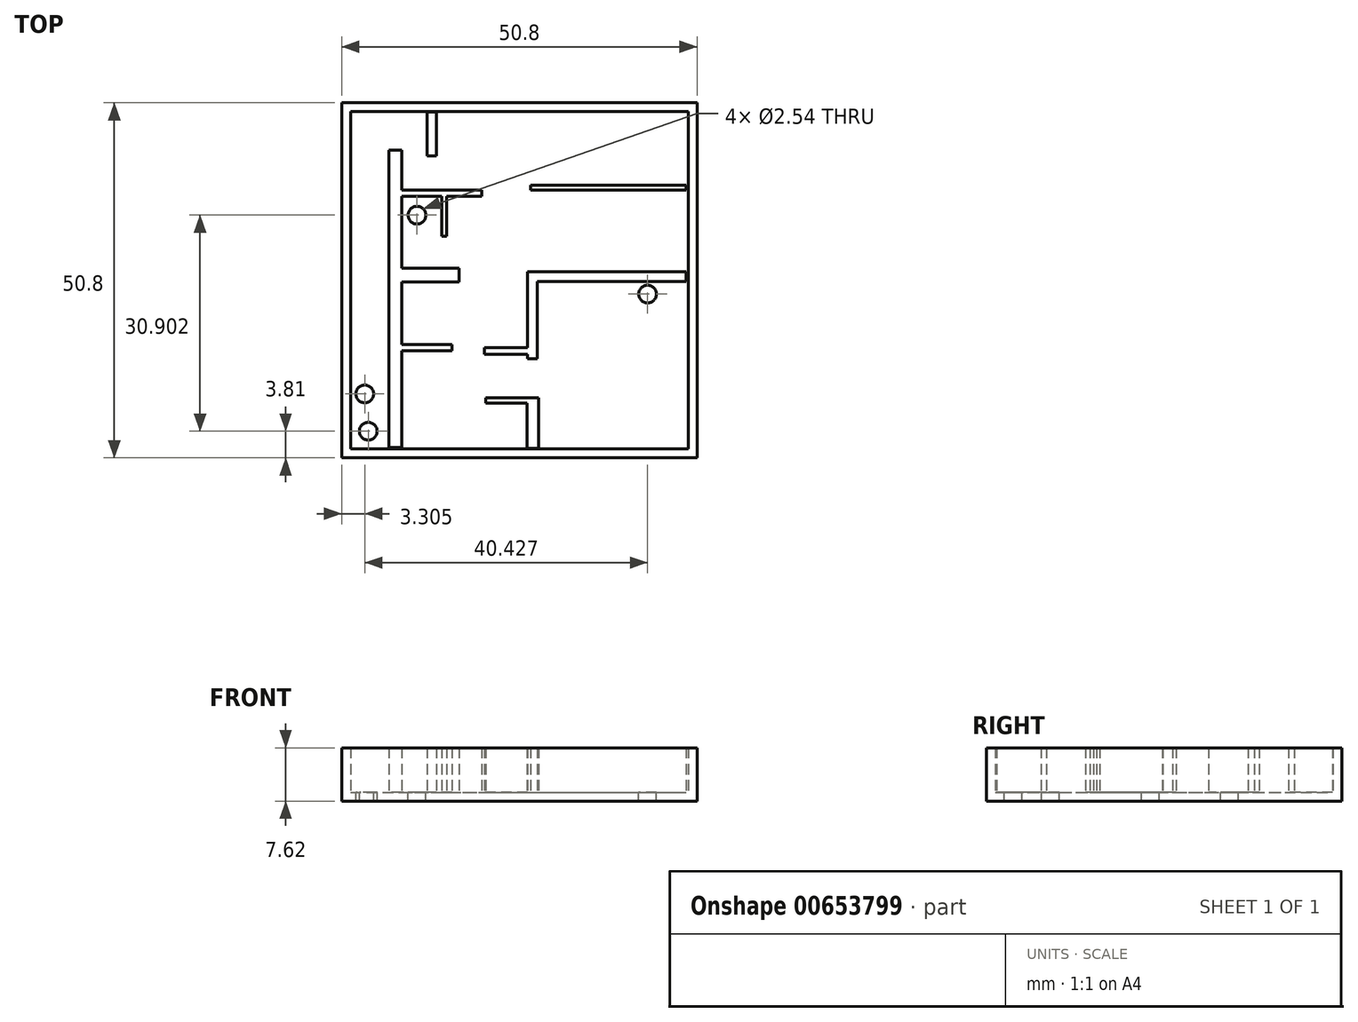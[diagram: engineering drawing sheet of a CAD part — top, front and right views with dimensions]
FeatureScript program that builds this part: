
annotation { "Feature Type Name" : "Feature", "Feature Type Description" : "" }
export const myFeature = defineFeature(function(context is Context, id is Id, definition is map)
    precondition{}
    {
        {
            var Q0;
            Q0=qCreatedBy(makeId("Top.planeOp"),FACE);
            var sketch = newSketch(context, id + "F0", { "sketchPlane" : qUnion([Q0])});
            skLineSegment(sketch, "E0.bottom", {"start": v(0, 0) * mm, "end": v(50.8, 0) * mm});
            skLineSegment(sketch, "E0.top", {"start": v(0, 50.8) * mm, "end": v(50.8, 50.8) * mm});
            skLineSegment(sketch, "E0.left", {"start": v(0, 0) * mm, "end": v(0, 50.8) * mm});
            skLineSegment(sketch, "E0.right", {"start": v(50.8, 0) * mm, "end": v(50.8, 50.8) * mm});
            skSolve(sketch);
        }
        {
            var Q0;
            Q0=makeQuery(id+"F0.imprint","IMPRINT",FACE,{"disambiguationData":[TD([[makeQuery(id+"F0.imprint","IMPRINT",EDGE,{"derivedFrom":sQuery(id+"F0.wireOp",EDGE,"E0.bottom")}),1.0]])]});
            extrude(context, id + "F1", {"entities" : qUnion([Q0]), "depth" : 7.62 * mm, "offsetDistance" : 25.4 * mm});
        }
        {
            var Q0;
            Q0=makeQuery(id+"F1.opExtrude","CAP_FACE",FACE,{"disambiguationData":[OSD([sQuery(id+"F0.wireOp",EDGE,"E0.bottom"),sQuery(id+"F0.wireOp",EDGE,"E0.top"),sQuery(id+"F0.wireOp",EDGE,"E0.left"),sQuery(id+"F0.wireOp",EDGE,"E0.right")])],"isStart":false});
            shell(context, id + "F2", {"entities" : qUnion([Q0]), "thickness" : 1.27 * mm});
        }
        {
            var Q0;
            Q0=makeQuery(id+"F2.opShell","OFFSET_FACE",FACE,{"disambiguationData":[OSD([sQuery(id+"F0.wireOp",EDGE,"E0.bottom"),sQuery(id+"F0.wireOp",EDGE,"E0.top"),sQuery(id+"F0.wireOp",EDGE,"E0.left"),sQuery(id+"F0.wireOp",EDGE,"E0.right")])]});
            var sketch = newSketch(context, id + "F3", { "sketchPlane" : qUnion([Q0])});
            skLineSegment(sketch, "E1", {"start": v(1.27, 1.27) * mm, "end": v(1.27, 3.81) * mm});
            skLineSegment(sketch, "E2", {"start": v(1.27, 3.81) * mm, "end": v(3.81, 3.81) * mm});
            skLineSegment(sketch, "E3", {"start": v(1.27, 1.27) * mm, "end": v(3.81, 1.27) * mm});
            skLineSegment(sketch, "E4", {"start": v(3.81, 1.27) * mm, "end": v(3.81, 3.81) * mm});
            skCircle(sketch, "E5", {"center": v(3.81, 3.81) * mm, "radius": 1.27 * mm});
            skSolve(sketch);
        }
        {
            var Q0;
            {var subQ0=sQuery(id+"F3.wireOp",EDGE,"E4");var subQ1=sQuery(id+"F3.wireOp",EDGE,"E2");var subQ2=makeQuery(id+"F3.imprint","INTERSECT",VERTEX,{"derivedFrom":[subQ1,subQ0]});Q0=makeQuery(id+"F3.imprint","IMPRINT",FACE,{"disambiguationData":[TD([[makeQuery(id+"F3.imprint","IMPRINT",EDGE,{"disambiguationData":[TD([[subQ2,1.0]])],"derivedFrom":subQ1}),1.0]])]});}
            var Q1;
            {var subQ0=sQuery(id+"F3.wireOp",EDGE,"E4");var subQ1=sQuery(id+"F3.wireOp",EDGE,"E2");var subQ2=makeQuery(id+"F3.imprint","INTERSECT",VERTEX,{"derivedFrom":[subQ1,subQ0]});Q1=makeQuery(id+"F3.imprint","IMPRINT",FACE,{"disambiguationData":[TD([[makeQuery(id+"F3.imprint","IMPRINT",EDGE,{"disambiguationData":[TD([[subQ2,1.0]])],"derivedFrom":subQ1}),-1.0]])]});}
            extrude(context, id + "F4", {"entities" : qUnion([Q0, Q1]), "operationType" : NewBodyOperationType.REMOVE, "oppositeDirection" : true, "depth" : 25.4 * mm, "offsetDistance" : 25.4 * mm});
        }
        {
            var Q0;
            {var subQ0=sQuery(id+"FkNisRUT37BZLC1_1.wireOp",EDGE,"DEcF1Pi9-BhNb-Ntu2-fWaS-qb82FBI6M594");Q0=makeQuery(id+"FkNisRUT37BZLC1_1.imprint","IMPRINT",FACE,{"disambiguationData":[TD([[makeQuery(id+"FkNisRUT37BZLC1_1.imprint","IMPRINT",EDGE,{"derivedFrom":subQ0}),-1.0]])]});}
            var Q1;
            {var subQ13=sQuery(id+"F0.wireOp",EDGE,"E0.top");var subQ14=makeQuery(id+"F2.opShell","OFFSET_EDGE",EDGE,{"disambiguationData":[OSD([subQ13]),TDD([makeQuery(id+"F1.opExtrude","CAP_EDGE",EDGE,{"disambiguationData":[OSD([subQ13])],"isStart":true})])]});Q1=makeQuery(id+"F3.imprint","IMPRINT",FACE,{"disambiguationData":[TD([[makeQuery(id+"F3.imprint","IMPRINT",EDGE,{"derivedFrom":subQ14}),-1.0]])]});}
            extrude(context, id + "F5", {"entities" : qUnion([Q0, Q1]), "operationType" : NewBodyOperationType.REMOVE, "depth" : 6.35 * mm, "offsetDistance" : 25.4 * mm});
        }
        {
            var Q0;
            {var subQ0=sQuery(id+"F3.wireOp",EDGE,"E4");var subQ1=sQuery(id+"F3.wireOp",EDGE,"E2");var subQ2=makeQuery(id+"F3.imprint","INTERSECT",VERTEX,{"derivedFrom":[subQ1,subQ0]});Q0=makeQuery(id+"F3.imprint","IMPRINT",FACE,{"disambiguationData":[TD([[makeQuery(id+"F3.imprint","IMPRINT",EDGE,{"disambiguationData":[TD([[subQ2,1.0]])],"derivedFrom":subQ1}),1.0]])]});}
            var Q1;
            {var subQ0=sQuery(id+"F3.wireOp",EDGE,"E4");var subQ1=sQuery(id+"F3.wireOp",EDGE,"E2");var subQ2=makeQuery(id+"F3.imprint","INTERSECT",VERTEX,{"derivedFrom":[subQ1,subQ0]});Q1=makeQuery(id+"F3.imprint","IMPRINT",FACE,{"disambiguationData":[TD([[makeQuery(id+"F3.imprint","IMPRINT",EDGE,{"disambiguationData":[TD([[subQ2,1.0]])],"derivedFrom":subQ1}),-1.0]])]});}
            extrude(context, id + "F6", {"entities" : qUnion([Q0, Q1]), "operationType" : NewBodyOperationType.REMOVE, "oppositeDirection" : true, "depth" : 25.4 * mm, "offsetDistance" : 25.4 * mm});
        }
        {
            var Q0;
            {var subQ13=sQuery(id+"F0.wireOp",EDGE,"E0.top");var subQ14=makeQuery(id+"F2.opShell","OFFSET_EDGE",EDGE,{"disambiguationData":[OSD([subQ13]),TDD([makeQuery(id+"F1.opExtrude","CAP_EDGE",EDGE,{"disambiguationData":[OSD([subQ13])],"isStart":true})])]});Q0=makeQuery(id+"F3.imprint","IMPRINT",FACE,{"disambiguationData":[TD([[makeQuery(id+"F3.imprint","IMPRINT",EDGE,{"derivedFrom":subQ14}),-1.0]])]});}
            var sketch = newSketch(context, id + "F7", { "sketchPlane" : qUnion([Q0])});
            skLineSegment(sketch, "E6.bottom", {"start": v(8.63, 1.49) * mm, "end": v(6.74, 1.49) * mm});
            skLineSegment(sketch, "E6.top", {"start": v(8.63, 44) * mm, "end": v(6.74, 44) * mm});
            skLineSegment(sketch, "E6.left", {"start": v(8.63, 1.49) * mm, "end": v(8.63, 44) * mm});
            skLineSegment(sketch, "E6.right", {"start": v(6.74, 1.49) * mm, "end": v(6.74, 44) * mm});
            skLineSegment(sketch, "E7.bottom", {"start": v(8.63, 38.28) * mm, "end": v(20.05, 38.28) * mm});
            skLineSegment(sketch, "E7.top", {"start": v(8.63, 37.44) * mm, "end": v(20.05, 37.44) * mm});
            skLineSegment(sketch, "E7.left", {"start": v(8.63, 38.28) * mm, "end": v(8.63, 37.44) * mm});
            skLineSegment(sketch, "E7.right", {"start": v(20.05, 38.28) * mm, "end": v(20.05, 37.44) * mm});
            skLineSegment(sketch, "E8.bottom", {"start": v(14.34, 37.44) * mm, "end": v(14.99, 37.44) * mm});
            skLineSegment(sketch, "E8.top", {"start": v(14.34, 31.73) * mm, "end": v(14.99, 31.73) * mm});
            skLineSegment(sketch, "E8.left", {"start": v(14.34, 37.44) * mm, "end": v(14.34, 31.73) * mm});
            skLineSegment(sketch, "E8.right", {"start": v(14.99, 37.44) * mm, "end": v(14.99, 31.73) * mm});
            skCircle(sketch, "E9", {"center": v(10.77, 34.71) * mm, "radius": 1.27 * mm});
            skCircle(sketch, "E10", {"center": v(3.3, 9.14) * mm, "radius": 1.27 * mm});
            skLineSegment(sketch, "E11", {"start": v(8.63, 27.12) * mm, "end": v(16.8, 27.12) * mm});
            skLineSegment(sketch, "E12", {"start": v(16.8, 27.12) * mm, "end": v(16.8, 25.95) * mm});
            skLineSegment(sketch, "E13", {"start": v(8.63, 25.17) * mm, "end": v(16.8, 25.17) * mm});
            skLineSegment(sketch, "E14", {"start": v(16.8, 25.95) * mm, "end": v(16.8, 25.17) * mm});
            skLineSegment(sketch, "E15.bottom", {"start": v(13.56, 49.5) * mm, "end": v(12.2, 49.5) * mm});
            skLineSegment(sketch, "E15.top", {"start": v(13.56, 43.21) * mm, "end": v(12.2, 43.21) * mm});
            skLineSegment(sketch, "E15.left", {"start": v(13.56, 49.5) * mm, "end": v(13.56, 43.21) * mm});
            skLineSegment(sketch, "E15.right", {"start": v(12.2, 49.5) * mm, "end": v(12.2, 43.21) * mm});
            skLineSegment(sketch, "E16.bottom", {"start": v(26.99, 39) * mm, "end": v(49.25, 39) * mm});
            skLineSegment(sketch, "E16.top", {"start": v(26.99, 38.28) * mm, "end": v(49.25, 38.28) * mm});
            skLineSegment(sketch, "E16.left", {"start": v(26.99, 39) * mm, "end": v(26.99, 38.28) * mm});
            skLineSegment(sketch, "E16.right", {"start": v(49.25, 39) * mm, "end": v(49.25, 38.28) * mm});
            skLineSegment(sketch, "E17.bottom", {"start": v(26.6, 26.6) * mm, "end": v(27.96, 26.6) * mm});
            skLineSegment(sketch, "E17.top", {"start": v(26.6, 14.14) * mm, "end": v(27.96, 14.14) * mm});
            skLineSegment(sketch, "E17.left", {"start": v(26.6, 26.6) * mm, "end": v(26.6, 14.14) * mm});
            skLineSegment(sketch, "E17.right", {"start": v(27.96, 26.6) * mm, "end": v(27.96, 14.14) * mm});
            skLineSegment(sketch, "E18.bottom", {"start": v(27.96, 26.6) * mm, "end": v(49.25, 26.6) * mm});
            skLineSegment(sketch, "E18.top", {"start": v(27.96, 25.24) * mm, "end": v(49.25, 25.24) * mm});
            skLineSegment(sketch, "E18.left", {"start": v(27.96, 26.6) * mm, "end": v(27.96, 25.24) * mm});
            skLineSegment(sketch, "E18.right", {"start": v(49.25, 26.6) * mm, "end": v(49.25, 25.24) * mm});
            skCircle(sketch, "E19", {"center": v(43.73, 23.42) * mm, "radius": 1.27 * mm});
            skLineSegment(sketch, "E20.bottom", {"start": v(26.51, 8.57) * mm, "end": v(28.15, 8.57) * mm});
            skLineSegment(sketch, "E20.top", {"start": v(26.51, 1.37) * mm, "end": v(28.15, 1.37) * mm});
            skLineSegment(sketch, "E20.left", {"start": v(26.51, 8.57) * mm, "end": v(26.51, 1.37) * mm});
            skLineSegment(sketch, "E20.right", {"start": v(28.15, 8.57) * mm, "end": v(28.15, 1.37) * mm});
            skLineSegment(sketch, "E21.bottom", {"start": v(26.6, 14.8) * mm, "end": v(20.4, 14.8) * mm});
            skLineSegment(sketch, "E21.top", {"start": v(26.6, 15.78) * mm, "end": v(20.4, 15.78) * mm});
            skLineSegment(sketch, "E21.left", {"start": v(26.6, 14.8) * mm, "end": v(26.6, 15.78) * mm});
            skLineSegment(sketch, "E21.right", {"start": v(20.4, 14.8) * mm, "end": v(20.4, 15.78) * mm});
            skLineSegment(sketch, "E22.bottom", {"start": v(20.62, 8.57) * mm, "end": v(26.51, 8.57) * mm});
            skLineSegment(sketch, "E22.top", {"start": v(20.62, 7.81) * mm, "end": v(26.51, 7.81) * mm});
            skLineSegment(sketch, "E22.left", {"start": v(20.62, 8.57) * mm, "end": v(20.62, 7.81) * mm});
            skLineSegment(sketch, "E22.right", {"start": v(26.51, 8.57) * mm, "end": v(26.51, 7.81) * mm});
            skLineSegment(sketch, "E23.bottom", {"start": v(15.76, 16.21) * mm, "end": v(8.63, 16.21) * mm});
            skLineSegment(sketch, "E23.top", {"start": v(15.76, 15.29) * mm, "end": v(8.63, 15.29) * mm});
            skLineSegment(sketch, "E23.left", {"start": v(15.76, 16.21) * mm, "end": v(15.76, 15.29) * mm});
            skLineSegment(sketch, "E23.right", {"start": v(8.63, 16.21) * mm, "end": v(8.63, 15.29) * mm});
            skSolve(sketch);
        }
        {
            var Q0;
            {var subQ3=sQuery(id+"F7.wireOp",EDGE,"E6.bottom");Q0=makeQuery(id+"F7.imprint","IMPRINT",FACE,{"disambiguationData":[TD([[makeQuery(id+"F7.imprint","IMPRINT",EDGE,{"derivedFrom":subQ3}),-1.0]])]});}
            extrude(context, id + "F8", {"entities" : qUnion([Q0]), "operationType" : NewBodyOperationType.ADD, "depth" : 6.35 * mm, "offsetDistance" : 25.4 * mm});
        }
        {
            var Q0;
            Q0 = qSketchRegion(id + "FkNisRUT37BZLC1_1", true);
            var Q1;
            Q1 = qSketchRegion(id + "F7", true);
            extrude(context, id + "F9", {"entities" : qUnion([Q0, Q1]), "operationType" : NewBodyOperationType.ADD, "depth" : 6.35 * mm, "offsetDistance" : 25.4 * mm});
        }
        {
            var Q0;
            Q0=makeQuery(id+"F9.opExtrude","CAP_FACE",FACE,{"disambiguationData":[OSD([sQuery(id+"F7.wireOp",EDGE,"E9")])],"isStart":false});
            var Q1;
            Q1=makeQuery(id+"F9.opExtrude","CAP_FACE",FACE,{"disambiguationData":[OSD([sQuery(id+"F7.wireOp",EDGE,"E10")])],"isStart":false});
            extrude(context, id + "F10", {"entities" : qUnion([Q0, Q1]), "operationType" : NewBodyOperationType.REMOVE, "oppositeDirection" : true, "depth" : 25.4 * mm, "offsetDistance" : 25.4 * mm});
        }
        {
            var Q0;
            Q0=makeQuery(id+"F9.opExtrude","CAP_FACE",FACE,{"disambiguationData":[OSD([sQuery(id+"F7.wireOp",EDGE,"E19")])],"isStart":false});
            extrude(context, id + "F11", {"entities" : qUnion([Q0]), "operationType" : NewBodyOperationType.REMOVE, "oppositeDirection" : true, "depth" : 25.4 * mm, "offsetDistance" : 25.4 * mm});
        }
    });
